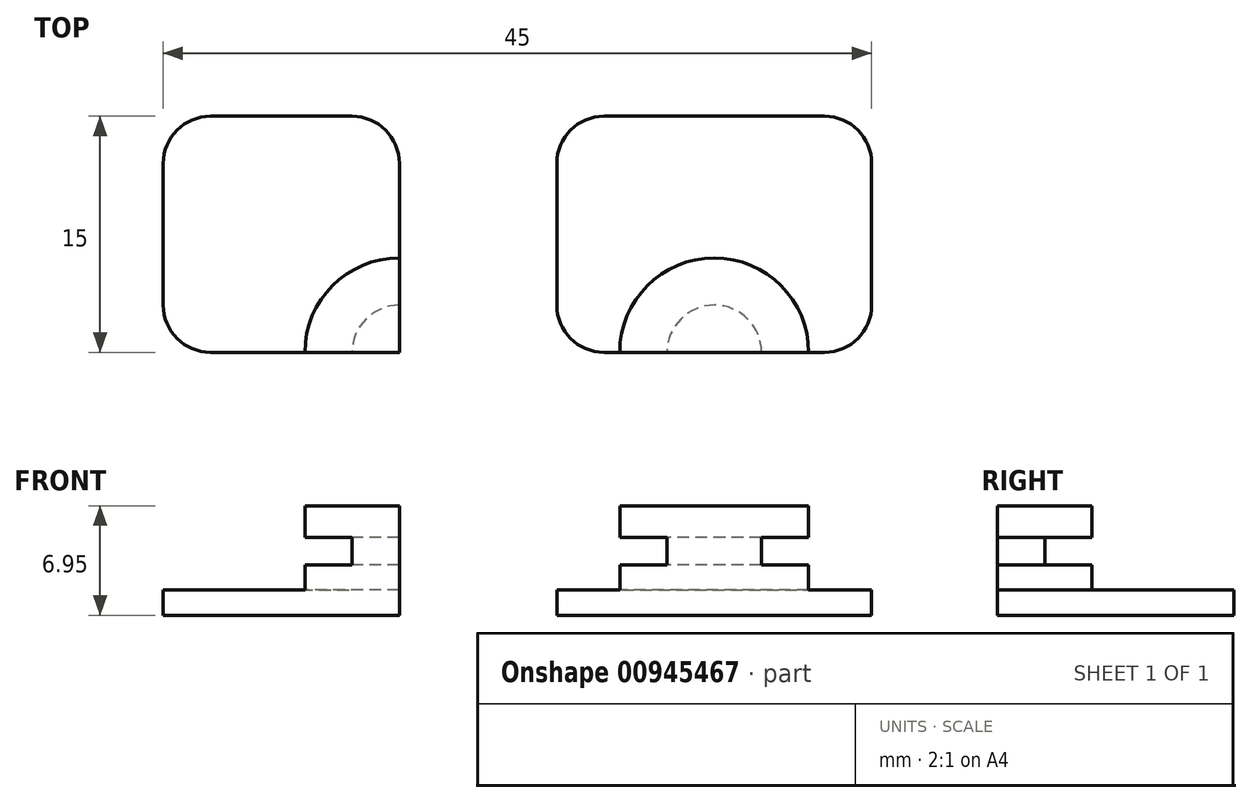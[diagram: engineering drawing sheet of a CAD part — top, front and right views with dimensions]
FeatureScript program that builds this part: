
annotation { "Feature Type Name" : "Feature", "Feature Type Description" : "" }
export const myFeature = defineFeature(function(context is Context, id is Id, definition is map)
    precondition{}
    {
        {
            var Q0;
            Q0=qCreatedBy(makeId("Top.planeOp"),FACE);
            var sketch = newSketch(context, id + "F0", { "sketchPlane" : qUnion([Q0])});
            skLineSegment(sketch, "E0.bottom", {"start": v(3, 0) * mm, "end": v(12, 0) * mm});
            skLineSegment(sketch, "E0.top", {"start": v(3, -15) * mm, "end": v(15, -15) * mm});
            skLineSegment(sketch, "E0.left", {"start": v(0, -3) * mm, "end": v(0, -12) * mm});
            skLineSegment(sketch, "E0.right", {"start": v(15, -3) * mm, "end": v(15, -15) * mm});
            skArc(sketch, "E1", {"start": v(15, -12) * mm, "mid": v(12.88, -12.88) * mm, "end": v(12, -15) * mm});
            skArc(sketch, "E2", {"start": v(15, -9) * mm, "mid": v(10.76, -10.76) * mm, "end": v(9, -15) * mm});
            skPoint(sketch, "E3.visualSharp", {"position": v(15, 0) * mm});
            skArc(sketch, "E3.filletArc", {"start": v(15, -3) * mm, "mid": v(14.12, -0.88) * mm, "end": v(12, 0) * mm});
            skPoint(sketch, "E4.visualSharp", {"position": v(0, 0) * mm});
            skArc(sketch, "E4.filletArc", {"start": v(3, 0) * mm, "mid": v(0.88, -0.88) * mm, "end": v(0, -3) * mm});
            skPoint(sketch, "E5.visualSharp", {"position": v(0, -15) * mm});
            skArc(sketch, "E5.filletArc", {"start": v(0, -12) * mm, "mid": v(0.88, -14.12) * mm, "end": v(3, -15) * mm});
            skLineSegment(sketch, "E6.bottom", {"start": v(28, 0) * mm, "end": v(42, 0) * mm});
            skLineSegment(sketch, "E6.top", {"start": v(28, -15) * mm, "end": v(42, -15) * mm});
            skLineSegment(sketch, "E6.left", {"start": v(25, -3) * mm, "end": v(25, -12) * mm});
            skLineSegment(sketch, "E6.right", {"start": v(45, -3) * mm, "end": v(45, -12) * mm});
            skPoint(sketch, "E7.visualSharp", {"position": v(25, 0) * mm});
            skArc(sketch, "E7.filletArc", {"start": v(28, 0) * mm, "mid": v(25.88, -0.88) * mm, "end": v(25, -3) * mm});
            skPoint(sketch, "E8.visualSharp", {"position": v(45, 0) * mm});
            skArc(sketch, "E8.filletArc", {"start": v(45, -3) * mm, "mid": v(44.12, -0.88) * mm, "end": v(42, 0) * mm});
            skPoint(sketch, "E9.visualSharp", {"position": v(25, -15) * mm});
            skArc(sketch, "E9.filletArc", {"start": v(25, -12) * mm, "mid": v(25.88, -14.12) * mm, "end": v(28, -15) * mm});
            skPoint(sketch, "E10.visualSharp", {"position": v(45, -15) * mm});
            skArc(sketch, "E10.filletArc", {"start": v(42, -15) * mm, "mid": v(44.12, -14.12) * mm, "end": v(45, -12) * mm});
            skArc(sketch, "E11", {"start": v(38, -15) * mm, "mid": v(35, -12) * mm, "end": v(32, -15) * mm});
            skArc(sketch, "E12", {"start": v(41, -15) * mm, "mid": v(35, -9) * mm, "end": v(29, -15) * mm});
            skSolve(sketch);
        }
        {
            assignVariable(context, id + "F1", {"name" : "thk", "anyValue" : 1.6});
        }
        {
            assignVariable(context, id + "F2", {"name" : "ht", "anyValue" : 3.2});
        }
        {
            assignVariable(context, id + "F3", {"name" : "pcb", "anyValue" : 1.75});
        }
        {
            assignVariable(context, id + "F4", {"name" : "top", "anyValue" : 2});
        }
        {
            var Q0;
            Q0=makeQuery(id+"F0.imprint","IMPRINT",FACE,{"disambiguationData":[TD([[makeQuery(id+"F0.imprint","IMPRINT",EDGE,{"derivedFrom":sQuery(id+"F0.wireOp",EDGE,"E0.bottom")}),-1.0]])]});
            var Q1;
            Q1=makeQuery(id+"F0.imprint","IMPRINT",FACE,{"disambiguationData":[TD([[makeQuery(id+"F0.imprint","IMPRINT",EDGE,{"derivedFrom":sQuery(id+"F0.wireOp",EDGE,"E6.bottom")}),-1.0]])]});
            extrude(context, id + "F5", {"entities" : qUnion([Q0, Q1]), "depth" : (getVariable(context, 'thk')) * mm, "offsetDistance" : 25 * mm});
        }
        {
            var Q0;
            {var subQ0=sQuery(id+"F0.wireOp",EDGE,"E1");Q0=makeQuery(id+"F0.imprint","IMPRINT",FACE,{"disambiguationData":[TD([[makeQuery(id+"F0.imprint","IMPRINT",EDGE,{"derivedFrom":subQ0}),-1.0]])]});}
            var Q1;
            {var subQ0=sQuery(id+"F0.wireOp",EDGE,"E11");Q1=makeQuery(id+"F0.imprint","IMPRINT",FACE,{"disambiguationData":[TD([[makeQuery(id+"F0.imprint","IMPRINT",EDGE,{"derivedFrom":subQ0}),-1.0]])]});}
            extrude(context, id + "F6", {"entities" : qUnion([Q0, Q1]), "operationType" : NewBodyOperationType.ADD, "depth" : (getVariable(context, 'ht')) * mm, "offsetDistance" : 25 * mm});
        }
        {
            var Q0;
            {var subQ3=sQuery(id+"F0.wireOp",EDGE,"E1");Q0=makeQuery(id+"F0.imprint","IMPRINT",FACE,{"disambiguationData":[TD([[makeQuery(id+"F0.imprint","IMPRINT",EDGE,{"derivedFrom":subQ3}),1.0]])]});}
            var Q1;
            {var subQ0=sQuery(id+"F0.wireOp",EDGE,"E11");Q1=makeQuery(id+"F0.imprint","IMPRINT",FACE,{"disambiguationData":[TD([[makeQuery(id+"F0.imprint","IMPRINT",EDGE,{"derivedFrom":subQ0}),1.0]])]});}
            extrude(context, id + "F7", {"entities" : qUnion([Q0, Q1]), "operationType" : NewBodyOperationType.ADD, "depth" : (getVariable(context, 'ht') + getVariable(context, 'pcb') + getVariable(context, 'top')) * mm, "offsetDistance" : 25 * mm});
        }
        {
            var Q0;
            {var subQ0=sQuery(id+"F0.wireOp",EDGE,"E1");Q0=makeQuery(id+"F0.imprint","IMPRINT",FACE,{"disambiguationData":[TD([[makeQuery(id+"F0.imprint","IMPRINT",EDGE,{"derivedFrom":subQ0}),-1.0]])]});}
            var Q1;
            {var subQ0=sQuery(id+"F0.wireOp",EDGE,"E11");Q1=makeQuery(id+"F0.imprint","IMPRINT",FACE,{"disambiguationData":[TD([[makeQuery(id+"F0.imprint","IMPRINT",EDGE,{"derivedFrom":subQ0}),-1.0]])]});}
            extrude(context, id + "F8", {"entities" : qUnion([Q0, Q1]), "operationType" : NewBodyOperationType.ADD, "depth" : (getVariable(context, 'ht') + getVariable(context, 'pcb') + getVariable(context, 'top')) * mm, "offsetDistance" : 25 * mm, "hasSecondDirection" : true, "secondDirectionOppositeDirection" : false, "secondDirectionDepth" : (getVariable(context, 'ht') + getVariable(context, 'pcb')) * mm});
        }
    });
